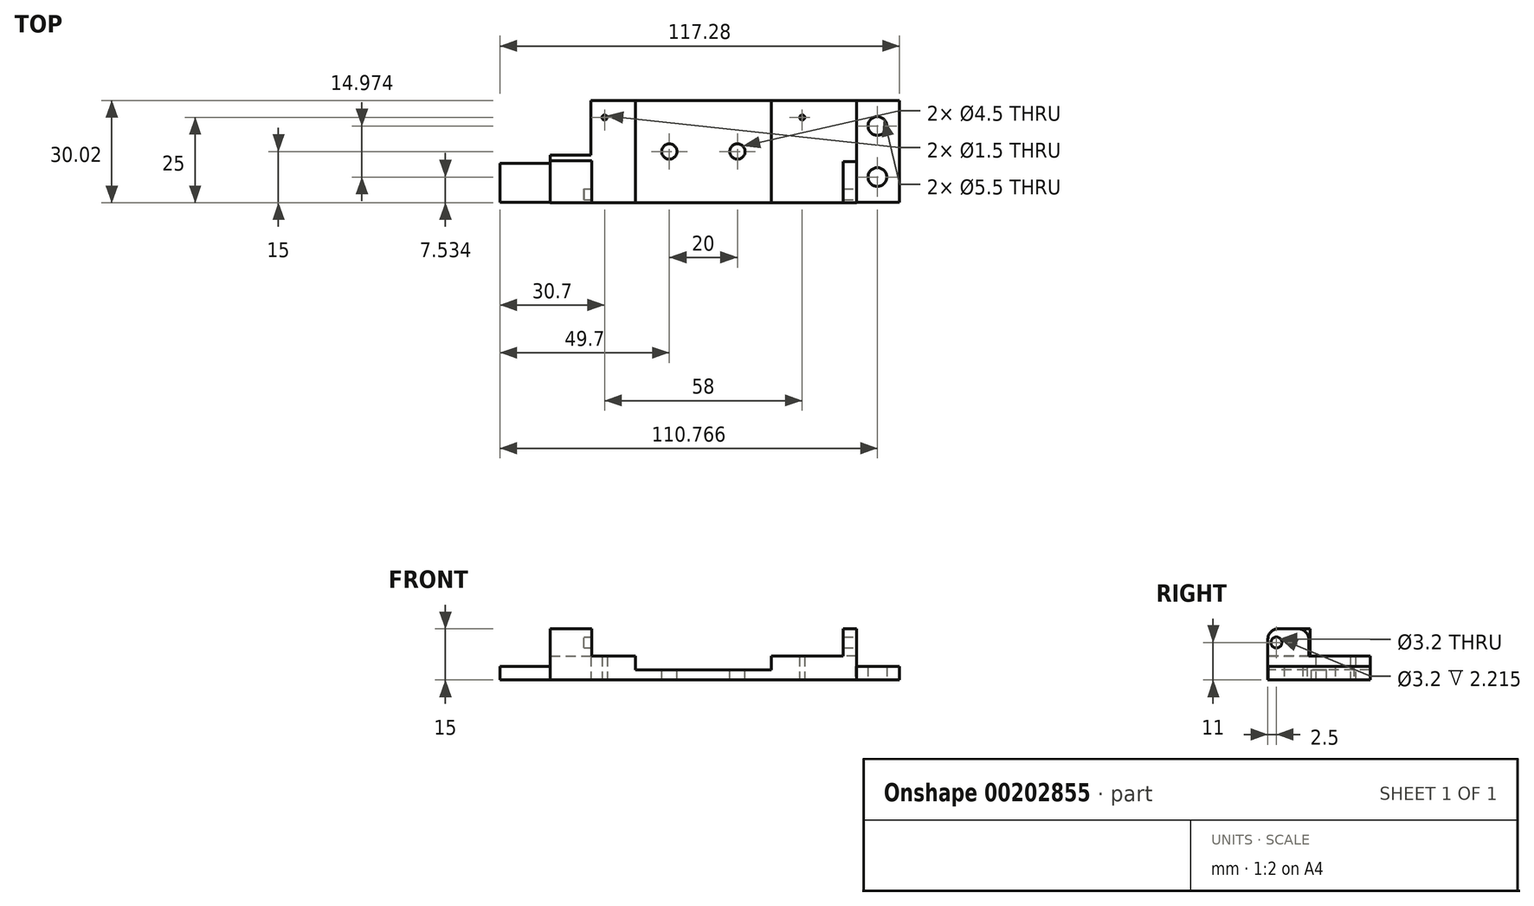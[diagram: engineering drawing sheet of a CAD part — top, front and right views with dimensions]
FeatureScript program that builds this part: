
annotation { "Feature Type Name" : "Feature", "Feature Type Description" : "" }
export const myFeature = defineFeature(function(context is Context, id is Id, definition is map)
    precondition{}
    {
        {
            var Q0;
            Q0=qCreatedBy(makeId("Top.planeOp"),FACE);
            var sketch = newSketch(context, id + "F0", { "sketchPlane" : qUnion([Q0])});
            skLineSegment(sketch, "E0.bottom", {"start": v(-45, 15) * mm, "end": v(45, 15) * mm});
            skLineSegment(sketch, "E0.top", {"start": v(-45, -15) * mm, "end": v(45, -15) * mm});
            skLineSegment(sketch, "E0.left", {"start": v(-45, 15) * mm, "end": v(-45, -15) * mm});
            skLineSegment(sketch, "E0.right", {"start": v(45, 15) * mm, "end": v(45, -15) * mm});
            skPoint(sketch, "E0.middle", {"position": v(0, 0) * mm});
            skLineSegment(sketch, "E1.bottom", {"start": v(-45, 15) * mm, "end": v(-33, 15) * mm});
            skLineSegment(sketch, "E1.top", {"start": v(-45, -1) * mm, "end": v(-33, -1) * mm});
            skLineSegment(sketch, "E1.left", {"start": v(-45, 15) * mm, "end": v(-45, -1) * mm});
            skLineSegment(sketch, "E1.right", {"start": v(-33, 15) * mm, "end": v(-33, -1) * mm});
            skLineSegment(sketch, "E2", {"start": v(45, 15) * mm, "end": v(29, 15) * mm});
            skLineSegment(sketch, "E3", {"start": v(29, 15) * mm, "end": v(29, 10) * mm});
            skLineSegment(sketch, "E4", {"start": v(-33, 15) * mm, "end": v(-29, 15) * mm});
            skLineSegment(sketch, "E5", {"start": v(-29, 15) * mm, "end": v(-29, 10) * mm});
            skCircle(sketch, "E6", {"center": v(-29, 10) * mm, "radius": 0.75 * mm});
            skCircle(sketch, "E7", {"center": v(29, 10) * mm, "radius": 0.75 * mm});
            skSolve(sketch);
        }
        {
            var Q0;
            Q0=makeQuery(id+"F0.imprint","IMPRINT",FACE,{"disambiguationData":[TD([[makeQuery(id+"F0.imprint","IMPRINT",EDGE,{"derivedFrom":sQuery(id+"F0.wireOp",EDGE,"E0.bottom")}),-1.0]])]});
            extrude(context, id + "F1", {"entities" : qUnion([Q0]), "depth" : 7 * mm});
        }
        {
            var Q0;
            Q0=makeQuery(id+"F1.opExtrude","CAP_FACE",FACE,{"disambiguationData":[OSD([sQuery(id+"F0.wireOp",EDGE,"E0.bottom"),sQuery(id+"F0.wireOp",EDGE,"E0.top"),sQuery(id+"F0.wireOp",EDGE,"E0.left"),sQuery(id+"F0.wireOp",EDGE,"E0.right"),sQuery(id+"F0.wireOp",EDGE,"E1.top"),sQuery(id+"F0.wireOp",EDGE,"E1.right"),sQuery(id+"F0.wireOp",EDGE,"E2"),sQuery(id+"F0.wireOp",EDGE,"E4"),sQuery(id+"F0.wireOp",EDGE,"E6"),sQuery(id+"F0.wireOp",EDGE,"E7")])],"isStart":false});
            var sketch = newSketch(context, id + "F2", { "sketchPlane" : qUnion([Q0])});
            skLineSegment(sketch, "E8.bottom", {"start": v(-45, -1) * mm, "end": v(-32.79, -1) * mm});
            skLineSegment(sketch, "E8.top", {"start": v(-45, -15) * mm, "end": v(-32.79, -15) * mm});
            skLineSegment(sketch, "E8.left", {"start": v(-45, -1) * mm, "end": v(-45, -15) * mm});
            skLineSegment(sketch, "E8.right", {"start": v(-32.79, -1) * mm, "end": v(-32.79, -15) * mm});
            skLineSegment(sketch, "E9.bottom", {"start": v(45, -15) * mm, "end": v(41, -15) * mm});
            skLineSegment(sketch, "E9.top", {"start": v(45, -3) * mm, "end": v(41, -3) * mm});
            skLineSegment(sketch, "E9.left", {"start": v(45, -15) * mm, "end": v(45, -3) * mm});
            skLineSegment(sketch, "E9.right", {"start": v(41, -15) * mm, "end": v(41, -3) * mm});
            skSolve(sketch);
        }
        {
            var Q0;
            Q0=makeQuery(id+"F2.imprint","IMPRINT",FACE,{"disambiguationData":[TD([[makeQuery(id+"F2.imprint","IMPRINT",EDGE,{"derivedFrom":sQuery(id+"F2.wireOp",EDGE,"E8.top")}),1.0]])]});
            var Q1;
            Q1=makeQuery(id+"F2.imprint","IMPRINT",FACE,{"disambiguationData":[TD([[makeQuery(id+"F2.imprint","IMPRINT",EDGE,{"derivedFrom":sQuery(id+"F2.wireOp",EDGE,"E9.bottom")}),1.0]])]});
            extrude(context, id + "F3", {"entities" : qUnion([Q0, Q1]), "operationType" : NewBodyOperationType.ADD, "depth" : 8 * mm});
        }
        {
            var Q0;
            Q0=makeQuery(id+"F3.opExtrude","CAP_FACE",FACE,{"disambiguationData":[OSD([sQuery(id+"F2.wireOp",EDGE,"E8.bottom"),sQuery(id+"F2.wireOp",EDGE,"E8.top"),sQuery(id+"F2.wireOp",EDGE,"E8.left"),sQuery(id+"F2.wireOp",EDGE,"E8.right")])],"isStart":false});
            var sketch = newSketch(context, id + "F4", { "sketchPlane" : qUnion([Q0])});
            skLineSegment(sketch, "E10.bottom", {"start": v(-45, -1) * mm, "end": v(-32.79, -1) * mm});
            skLineSegment(sketch, "E10.top", {"start": v(-45, -2.64) * mm, "end": v(-32.79, -2.64) * mm});
            skLineSegment(sketch, "E10.left", {"start": v(-45, -1) * mm, "end": v(-45, -2.64) * mm});
            skLineSegment(sketch, "E10.right", {"start": v(-32.79, -1) * mm, "end": v(-32.79, -2.64) * mm});
            skSolve(sketch);
        }
        {
            var Q0;
            Q0 = qSketchRegion(id + "F4", true);
            extrude(context, id + "F5", {"entities" : qUnion([Q0]), "operationType" : NewBodyOperationType.REMOVE, "oppositeDirection" : true, "depth" : 8 * mm});
        }
        {
            var Q0;
            Q0=makeQuery(id+"F3.boolean.opBoolean","MERGE",FACE,{"derivedFrom":[makeQuery(id+"F1.opExtrude","SWEPT_FACE",FACE,{"disambiguationData":[OSD([sQuery(id+"F0.wireOp",EDGE,"E0.right")])]}),makeQuery(id+"F3.opExtrude","SWEPT_FACE",FACE,{"disambiguationData":[OSD([sQuery(id+"F2.wireOp",EDGE,"E9.left")])]})]});
            var sketch = newSketch(context, id + "F6", { "sketchPlane" : qUnion([Q0])});
            skLineSegment(sketch, "E11", {"start": v(-15, 7) * mm, "end": v(-12.5, 7) * mm});
            skLineSegment(sketch, "E12", {"start": v(-12.5, 7) * mm, "end": v(-12.5, 11) * mm});
            skCircle(sketch, "E13", {"center": v(-12.5, 11) * mm, "radius": 1.6 * mm});
            skSolve(sketch);
        }
        {
            var Q0;
            Q0 = qSketchRegion(id + "F6", true);
            extrude(context, id + "F7", {"entities" : qUnion([Q0]), "operationType" : NewBodyOperationType.REMOVE, "oppositeDirection" : true, "depth" : 80 * mm});
        }
        {
            var Q0;
            Q0=makeQuery(id+"F5.boolean.opBoolean","MERGE",FACE,{"derivedFrom":[makeQuery(id+"F1.opExtrude","CAP_FACE",FACE,{"disambiguationData":[OSD([sQuery(id+"F0.wireOp",EDGE,"E0.bottom"),sQuery(id+"F0.wireOp",EDGE,"E0.top"),sQuery(id+"F0.wireOp",EDGE,"E0.left"),sQuery(id+"F0.wireOp",EDGE,"E0.right"),sQuery(id+"F0.wireOp",EDGE,"E1.top"),sQuery(id+"F0.wireOp",EDGE,"E1.right"),sQuery(id+"F0.wireOp",EDGE,"E2"),sQuery(id+"F0.wireOp",EDGE,"E4"),sQuery(id+"F0.wireOp",EDGE,"E6"),sQuery(id+"F0.wireOp",EDGE,"E7")])],"isStart":false}),makeQuery(id+"F5.opExtrude","CAP_FACE",FACE,{"disambiguationData":[OSD([sQuery(id+"F4.wireOp",EDGE,"E10.bottom"),sQuery(id+"F4.wireOp",EDGE,"E10.top"),sQuery(id+"F4.wireOp",EDGE,"E10.left"),sQuery(id+"F4.wireOp",EDGE,"E10.right")])],"isStart":false})]});
            var sketch = newSketch(context, id + "F8", { "sketchPlane" : qUnion([Q0])});
            skLineSegment(sketch, "E14", {"start": v(0, 0) * mm, "end": v(10, 0) * mm});
            skLineSegment(sketch, "E15", {"start": v(10, 0) * mm, "end": v(-10, 0) * mm});
            skPoint(sketch, "E15.endSnap0", {"position": v(5, 0) * mm});
            skCircle(sketch, "E16", {"center": v(-10, 0) * mm, "radius": 2.25 * mm});
            skCircle(sketch, "E17", {"center": v(10, 0) * mm, "radius": 2.25 * mm});
            skSolve(sketch);
        }
        {
            var Q0;
            Q0=makeQuery(id+"F8.imprint","IMPRINT",FACE,{"disambiguationData":[TD([[makeQuery(id+"F8.imprint","IMPRINT",EDGE,{"derivedFrom":sQuery(id+"F8.wireOp",EDGE,"E16")}),1.0]])]});
            var Q1;
            Q1=makeQuery(id+"F8.imprint","IMPRINT",FACE,{"disambiguationData":[TD([[makeQuery(id+"F8.imprint","IMPRINT",EDGE,{"derivedFrom":sQuery(id+"F8.wireOp",EDGE,"E17")}),1.0]])]});
            extrude(context, id + "F9", {"entities" : qUnion([Q0, Q1]), "operationType" : NewBodyOperationType.REMOVE, "oppositeDirection" : true, "depth" : 25 * mm});
        }
        {
            var Q0;
            Q0=makeQuery(id+"F5.boolean.opBoolean","MERGE",FACE,{"derivedFrom":[makeQuery(id+"F1.opExtrude","CAP_FACE",FACE,{"disambiguationData":[OSD([sQuery(id+"F0.wireOp",EDGE,"E0.bottom"),sQuery(id+"F0.wireOp",EDGE,"E0.top"),sQuery(id+"F0.wireOp",EDGE,"E0.left"),sQuery(id+"F0.wireOp",EDGE,"E0.right"),sQuery(id+"F0.wireOp",EDGE,"E1.top"),sQuery(id+"F0.wireOp",EDGE,"E1.right"),sQuery(id+"F0.wireOp",EDGE,"E2"),sQuery(id+"F0.wireOp",EDGE,"E4"),sQuery(id+"F0.wireOp",EDGE,"E6"),sQuery(id+"F0.wireOp",EDGE,"E7")])],"isStart":false}),makeQuery(id+"F5.opExtrude","CAP_FACE",FACE,{"disambiguationData":[OSD([sQuery(id+"F4.wireOp",EDGE,"E10.bottom"),sQuery(id+"F4.wireOp",EDGE,"E10.top"),sQuery(id+"F4.wireOp",EDGE,"E10.left"),sQuery(id+"F4.wireOp",EDGE,"E10.right")])],"isStart":false})]});
            var sketch = newSketch(context, id + "F10", { "sketchPlane" : qUnion([Q0])});
            skLineSegment(sketch, "E18.bottom", {"start": v(20, 15) * mm, "end": v(-20, 15) * mm});
            skLineSegment(sketch, "E18.top", {"start": v(20, -15) * mm, "end": v(-20, -15) * mm});
            skLineSegment(sketch, "E18.left", {"start": v(20, 15) * mm, "end": v(20, -15) * mm});
            skLineSegment(sketch, "E18.right", {"start": v(-20, 15) * mm, "end": v(-20, -15) * mm});
            skPoint(sketch, "E18.middle", {"position": v(0, 0) * mm});
            skSolve(sketch);
        }
        {
            var Q0;
            Q0=makeQuery(id+"F10.imprint","IMPRINT",FACE,{"disambiguationData":[TD([[makeQuery(id+"F10.imprint","IMPRINT",EDGE,{"derivedFrom":sQuery(id+"F10.wireOp",EDGE,"E18.bottom")}),-1.0]])]});
            extrude(context, id + "F11", {"entities" : qUnion([Q0]), "operationType" : NewBodyOperationType.REMOVE, "oppositeDirection" : true, "depth" : 4 * mm});
        }
        {
            var Q0;
            Q0=makeQuery(id+"F3.opExtrude","CAP_EDGE",EDGE,{"disambiguationData":[OSD([sQuery(id+"F2.wireOp",EDGE,"E8.top")])],"isStart":false});
            var Q1;
            Q1=makeQuery(id+"F3.opExtrude","CAP_EDGE",EDGE,{"disambiguationData":[OSD([sQuery(id+"F2.wireOp",EDGE,"E9.bottom")])],"isStart":false});
            var Q2;
            Q2=makeQuery(id+"F5.boolean.opBoolean","COPY",EDGE,{"derivedFrom":makeQuery(id+"F5.opExtrude","CAP_EDGE",EDGE,{"disambiguationData":[OSD([sQuery(id+"F4.wireOp",EDGE,"E10.top")])],"isStart":true})});
            var Q3;
            Q3=makeQuery(id+"F3.opExtrude","CAP_EDGE",EDGE,{"disambiguationData":[OSD([sQuery(id+"F2.wireOp",EDGE,"E9.top")])],"isStart":false});
            fillet(context, id + "F12", {"entities" : qUnion([Q0, Q1, Q2, Q3]), "radius" : 3 * mm, "tangentPropagation" : true, "allowEdgeOverflow" : false});
        }
        {
            var Q0;
            Q0=qCreatedBy(makeId("Top.planeOp"),FACE);
            var sketch = newSketch(context, id + "F13", { "sketchPlane" : qUnion([Q0])});
            skLineSegment(sketch, "E19.bottom", {"start": v(44.56, 15.02) * mm, "end": v(57.58, 15.02) * mm});
            skLineSegment(sketch, "E19.top", {"start": v(44.56, -14.93) * mm, "end": v(57.58, -14.93) * mm});
            skLineSegment(sketch, "E19.left", {"start": v(44.56, 15.02) * mm, "end": v(44.56, -14.93) * mm});
            skLineSegment(sketch, "E19.right", {"start": v(57.58, 15.02) * mm, "end": v(57.58, -14.93) * mm});
            skLineSegment(sketch, "E20", {"start": v(51.07, 15.02) * mm, "end": v(51.07, 0) * mm});
            skLineSegment(sketch, "E21", {"start": v(51.07, 0) * mm, "end": v(51.07, -14.93) * mm});
            skCircle(sketch, "E22", {"center": v(51.07, 7.5) * mm, "radius": 2.75 * mm});
            skCircle(sketch, "E23", {"center": v(51.07, -7.47) * mm, "radius": 2.75 * mm});
            skSolve(sketch);
        }
        {
            var Q0;
            {var subQ9=sQuery(id+"F13.wireOp",EDGE,"E19.right");Q0=makeQuery(id+"F13.imprint","IMPRINT",FACE,{"disambiguationData":[TD([[makeQuery(id+"F13.imprint","IMPRINT",EDGE,{"derivedFrom":subQ9}),-1.0]])]});}
            var Q1;
            {var subQ5=sQuery(id+"F13.wireOp",EDGE,"E19.left");Q1=makeQuery(id+"F13.imprint","IMPRINT",FACE,{"disambiguationData":[TD([[makeQuery(id+"F13.imprint","IMPRINT",EDGE,{"derivedFrom":subQ5}),1.0]])]});}
            extrude(context, id + "F14", {"entities" : qUnion([Q0, Q1]), "operationType" : NewBodyOperationType.ADD, "depth" : 4 * mm});
        }
        {
            var Q0;
            Q0=qCreatedBy(makeId("Top.planeOp"),FACE);
            var sketch = newSketch(context, id + "F15", { "sketchPlane" : qUnion([Q0])});
            skLineSegment(sketch, "E24.bottom", {"start": v(-44.7, -14.85) * mm, "end": v(-59.7, -14.85) * mm});
            skLineSegment(sketch, "E24.top", {"start": v(-44.7, -3.45) * mm, "end": v(-59.7, -3.45) * mm});
            skLineSegment(sketch, "E24.left", {"start": v(-44.7, -14.85) * mm, "end": v(-44.7, -3.45) * mm});
            skLineSegment(sketch, "E24.right", {"start": v(-59.7, -14.85) * mm, "end": v(-59.7, -3.45) * mm});
            skSolve(sketch);
        }
        {
            var Q0;
            Q0=makeQuery(id+"F15.imprint","IMPRINT",FACE,{"disambiguationData":[TD([[makeQuery(id+"F15.imprint","IMPRINT",EDGE,{"derivedFrom":sQuery(id+"F15.wireOp",EDGE,"E24.bottom")}),-1.0]])]});
            extrude(context, id + "F16", {"entities" : qUnion([Q0]), "operationType" : NewBodyOperationType.ADD, "depth" : 4 * mm});
        }
    });
